# Revit family: ATXHTLR-LGUSWCT
name_source: partatom
category: Lighting Fixtures
units: mm (PartAtom-declared; Revit-internal decimal feet)

## family parameters
Cut with Voids When Loaded = No
Host = Face
Light Source = No
Maintain Annotation Orientation = No
Part Type = Normal
Room Calculation Point = No
Round Connector Dimension = Use Diameter
Shared = No

## types (4) — shared parameters
Default Elevation = 4' - 0"
Lamp = LED
Manufacturer = BEGHELLI
Model = ATXHTLRUSWCT-CEILING MOUNT
Type Image = ATC-CT- IMAGE .jpg
Wattage Comments = 2 W

## per-type parameters (varying)
| type | HOUSING MATERIAL | LETTER MATERIAL |
| ATXHTLRUSWCT-WHITE-CEILING MOUNT | HOUSING MATERIAL WHITE | LETTER MATERIAL RED |
| ATXHTLGUSWCT-WHITE-CEILING MOUNT | HOUSING MATERIAL WHITE | LETTERS MATERIAL GREEN |
| ATXHTLGUSWCT-BLACK-CEILING MOUNT | HOUSING MATERIAL BLACK | LETTERS MATERIAL GREEN |
| ATXHTLRUSWCT-BLACK-CEILING MOUNT | HOUSING MATERIAL BLACK | LETTER MATERIAL RED |

## geometry (parser evidence)
native form markers: Sweep x13
no freeform markers — native parametric forms only
